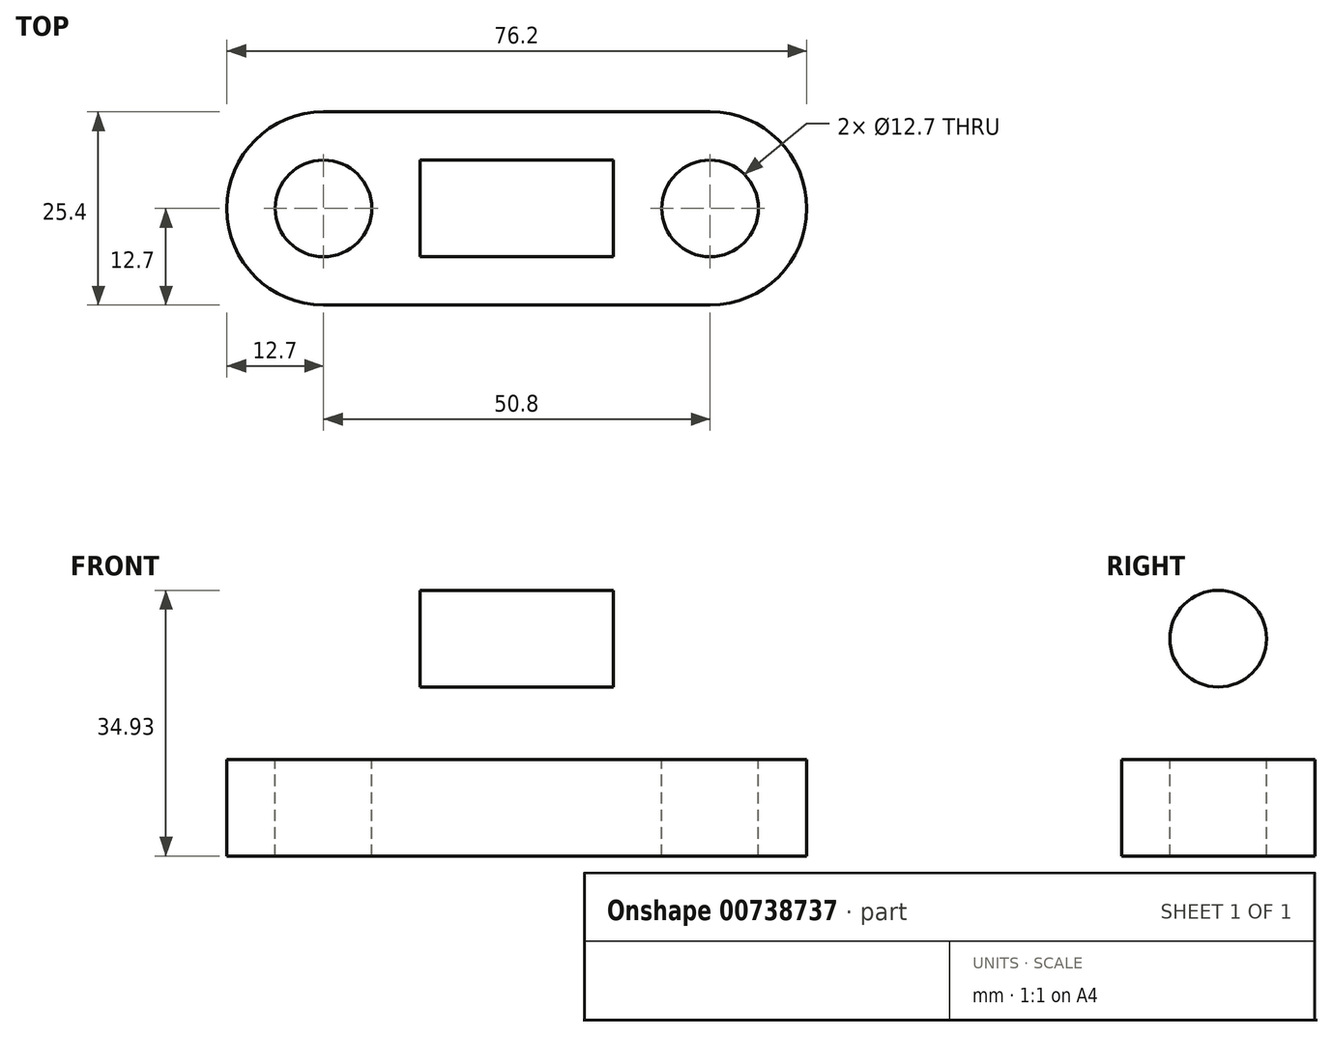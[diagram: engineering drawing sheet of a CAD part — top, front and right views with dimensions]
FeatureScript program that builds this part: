
annotation { "Feature Type Name" : "Feature", "Feature Type Description" : "" }
export const myFeature = defineFeature(function(context is Context, id is Id, definition is map)
    precondition{}
    {
        {
            var Q0;
            Q0=qCreatedBy(makeId("Front.planeOp"),FACE);
            var sketch = newSketch(context, id + "F0", { "sketchPlane" : qUnion([Q0])});
            skLineSegment(sketch, "E0", {"start": v(0, 0) * mm, "end": v(76.2, 0) * mm});
            skLineSegment(sketch, "E1", {"start": v(76.2, 0) * mm, "end": v(76.2, 12.7) * mm});
            skLineSegment(sketch, "E2", {"start": v(76.2, 12.7) * mm, "end": v(50.8, 12.7) * mm});
            skLineSegment(sketch, "E3", {"start": v(50.8, 12.7) * mm, "end": v(50.8, 44.45) * mm});
            skLineSegment(sketch, "E4", {"start": v(50.8, 44.45) * mm, "end": v(25.4, 44.45) * mm});
            skLineSegment(sketch, "E5", {"start": v(25.4, 44.45) * mm, "end": v(25.4, 12.7) * mm});
            skLineSegment(sketch, "E6", {"start": v(25.4, 12.7) * mm, "end": v(0, 12.7) * mm});
            skLineSegment(sketch, "E7", {"start": v(0, 12.7) * mm, "end": v(0, 0) * mm});
            skSolve(sketch);
        }
        {
            var Q0;
            Q0 = qSketchRegion(id + "F0", true);
            extrude(context, id + "F1", {"entities" : qUnion([Q0]), "depth" : 25.4 * mm, "offsetDistance" : 25.4 * mm});
        }
        {
            var Q0;
            Q0=makeQuery(id+"F1.opExtrude","SWEPT_FACE",FACE,{"disambiguationData":[OSD([sQuery(id+"F0.wireOp",EDGE,"E3")])]});
            var sketch = newSketch(context, id + "F2", { "sketchPlane" : qUnion([Q0])});
            skLineSegment(sketch, "E8", {"start": v(-25.4, 28.58) * mm, "end": v(0, 28.58) * mm});
            skCircle(sketch, "E9", {"center": v(-12.7, 28.58) * mm, "radius": 6.35 * mm});
            skArc(sketch, "E10", {"start": v(0, 28.58) * mm, "mid": v(-12.7, 41.27) * mm, "end": v(-25.4, 28.58) * mm});
            skSolve(sketch);
        }
        {
            var Q0;
            {var subQ0=sQuery(id+"F2.wireOp",EDGE,"E9");var subQ1=sQuery(id+"F2.wireOp",EDGE,"E8");var subQ2=makeQuery(id+"F2.imprint","INTERSECT",VERTEX,{"disambiguationData":[OD(0.0)],"derivedFrom":[subQ1,subQ0]});Q0=makeQuery(id+"F2.imprint","IMPRINT",FACE,{"disambiguationData":[TD([[makeQuery(id+"F2.imprint","IMPRINT",EDGE,{"disambiguationData":[TD([[subQ2,-1.0]])],"derivedFrom":subQ1}),1.0]])]});}
            var Q1;
            {var subQ0=sQuery(id+"F2.wireOp",EDGE,"E9");var subQ1=sQuery(id+"F2.wireOp",EDGE,"E8");var subQ2=makeQuery(id+"F2.imprint","INTERSECT",VERTEX,{"disambiguationData":[OD(0.0)],"derivedFrom":[subQ1,subQ0]});Q1=makeQuery(id+"F2.imprint","IMPRINT",FACE,{"disambiguationData":[TD([[makeQuery(id+"F2.imprint","IMPRINT",EDGE,{"disambiguationData":[TD([[subQ2,-1.0]])],"derivedFrom":subQ1}),-1.0]])]});}
            var Q2;
            {var subQ0=sQuery(id+"F2.wireOp",EDGE,"E10");Q2=makeQuery(id+"F2.imprint","IMPRINT",FACE,{"disambiguationData":[TD([[makeQuery(id+"F2.imprint","IMPRINT",EDGE,{"derivedFrom":subQ0}),-1.0]])]});}
            extrude(context, id + "F3", {"entities" : qUnion([Q0, Q1, Q2]), "operationType" : NewBodyOperationType.REMOVE, "endBound" : BoundingType.THROUGH_ALL, "oppositeDirection" : true, "depth" : 25.4 * mm, "offsetDistance" : 25.4 * mm});
        }
        {
            var Q0;
            Q0=makeQuery(id+"F1.opExtrude","SWEPT_FACE",FACE,{"disambiguationData":[OSD([sQuery(id+"F0.wireOp",EDGE,"E6")])]});
            var sketch = newSketch(context, id + "F4", { "sketchPlane" : qUnion([Q0])});
            skLineSegment(sketch, "E11", {"start": v(12.7, -25.4) * mm, "end": v(12.7, 0) * mm});
            skCircle(sketch, "E12", {"center": v(12.7, -12.7) * mm, "radius": 6.35 * mm});
            skArc(sketch, "E13", {"start": v(12.7, 0) * mm, "mid": v(0, -12.7) * mm, "end": v(12.7, -25.4) * mm});
            skSolve(sketch);
        }
        {
            var Q0;
            {var subQ0=sQuery(id+"F4.wireOp",EDGE,"E12");var subQ1=sQuery(id+"F4.wireOp",EDGE,"E11");var subQ2=makeQuery(id+"F4.imprint","INTERSECT",VERTEX,{"disambiguationData":[OD(0.0)],"derivedFrom":[subQ1,subQ0]});Q0=makeQuery(id+"F4.imprint","IMPRINT",FACE,{"disambiguationData":[TD([[makeQuery(id+"F4.imprint","IMPRINT",EDGE,{"disambiguationData":[TD([[subQ2,-1.0]])],"derivedFrom":subQ1}),1.0]])]});}
            var Q1;
            {var subQ0=sQuery(id+"F4.wireOp",EDGE,"E12");var subQ1=sQuery(id+"F4.wireOp",EDGE,"E11");var subQ2=makeQuery(id+"F4.imprint","INTERSECT",VERTEX,{"disambiguationData":[OD(0.0)],"derivedFrom":[subQ1,subQ0]});Q1=makeQuery(id+"F4.imprint","IMPRINT",FACE,{"disambiguationData":[TD([[makeQuery(id+"F4.imprint","IMPRINT",EDGE,{"disambiguationData":[TD([[subQ2,-1.0]])],"derivedFrom":subQ1}),-1.0]])]});}
            var Q2;
            {var subQ0=sQuery(id+"F4.wireOp",EDGE,"E13");var subQ1=sQuery(id+"F0.wireOp",EDGE,"E6");var subQ2=makeQuery(id+"F1.opExtrude","CAP_EDGE",EDGE,{"disambiguationData":[OSD([subQ1])],"isStart":true});var subQ3=makeQuery(id+"F4.imprint","INTERSECT",VERTEX,{"derivedFrom":[subQ2,sQuery(id+"F4.wireOp",EDGE,"E11"),subQ0]});Q2=makeQuery(id+"F4.imprint","IMPRINT",FACE,{"disambiguationData":[TD([[makeQuery(id+"F4.imprint","IMPRINT",EDGE,{"disambiguationData":[TD([[subQ3,-1.0]])],"derivedFrom":subQ0}),-1.0]])]});}
            var Q3;
            {var subQ0=sQuery(id+"F4.wireOp",EDGE,"E13");var subQ1=sQuery(id+"F0.wireOp",EDGE,"E6");var subQ2=makeQuery(id+"F1.opExtrude","CAP_EDGE",EDGE,{"disambiguationData":[OSD([subQ1])],"isStart":false});var subQ3=makeQuery(id+"F4.imprint","INTERSECT",VERTEX,{"derivedFrom":[subQ2,sQuery(id+"F4.wireOp",EDGE,"E11"),subQ0]});Q3=makeQuery(id+"F4.imprint","IMPRINT",FACE,{"disambiguationData":[TD([[makeQuery(id+"F4.imprint","IMPRINT",EDGE,{"disambiguationData":[TD([[subQ3,1.0]])],"derivedFrom":subQ0}),-1.0]])]});}
            extrude(context, id + "F5", {"entities" : qUnion([Q0, Q1, Q2, Q3]), "operationType" : NewBodyOperationType.REMOVE, "endBound" : BoundingType.THROUGH_ALL, "oppositeDirection" : true, "depth" : 25.4 * mm, "offsetDistance" : 25.4 * mm});
        }
        {
            var Q0;
            Q0=makeQuery(id+"F1.opExtrude","SWEPT_FACE",FACE,{"disambiguationData":[OSD([sQuery(id+"F0.wireOp",EDGE,"E2")])]});
            var sketch = newSketch(context, id + "F6", { "sketchPlane" : qUnion([Q0])});
            skLineSegment(sketch, "E14", {"start": v(63.5, 0) * mm, "end": v(63.5, -25.4) * mm});
            skCircle(sketch, "E15", {"center": v(63.5, -12.7) * mm, "radius": 6.35 * mm});
            skArc(sketch, "E16", {"start": v(63.5, -25.4) * mm, "mid": v(76.2, -12.7) * mm, "end": v(63.5, 0) * mm});
            skSolve(sketch);
        }
        {
            var Q0;
            {var subQ0=sQuery(id+"F6.wireOp",EDGE,"E15");var subQ1=sQuery(id+"F6.wireOp",EDGE,"E14");var subQ2=makeQuery(id+"F6.imprint","INTERSECT",VERTEX,{"disambiguationData":[OD(0.0)],"derivedFrom":[subQ1,subQ0]});Q0=makeQuery(id+"F6.imprint","IMPRINT",FACE,{"disambiguationData":[TD([[makeQuery(id+"F6.imprint","IMPRINT",EDGE,{"disambiguationData":[TD([[subQ2,-1.0]])],"derivedFrom":subQ1}),-1.0]])]});}
            var Q1;
            {var subQ0=sQuery(id+"F6.wireOp",EDGE,"E15");var subQ1=sQuery(id+"F6.wireOp",EDGE,"E14");var subQ2=makeQuery(id+"F6.imprint","INTERSECT",VERTEX,{"disambiguationData":[OD(0.0)],"derivedFrom":[subQ1,subQ0]});Q1=makeQuery(id+"F6.imprint","IMPRINT",FACE,{"disambiguationData":[TD([[makeQuery(id+"F6.imprint","IMPRINT",EDGE,{"disambiguationData":[TD([[subQ2,-1.0]])],"derivedFrom":subQ1}),1.0]])]});}
            var Q2;
            {var subQ0=sQuery(id+"F6.wireOp",EDGE,"E16");var subQ1=sQuery(id+"F0.wireOp",EDGE,"E2");var subQ2=makeQuery(id+"F1.opExtrude","CAP_EDGE",EDGE,{"disambiguationData":[OSD([subQ1])],"isStart":true});var subQ3=makeQuery(id+"F6.imprint","INTERSECT",VERTEX,{"derivedFrom":[subQ2,sQuery(id+"F6.wireOp",EDGE,"E14"),subQ0]});Q2=makeQuery(id+"F6.imprint","IMPRINT",FACE,{"disambiguationData":[TD([[makeQuery(id+"F6.imprint","IMPRINT",EDGE,{"disambiguationData":[TD([[subQ3,1.0]])],"derivedFrom":subQ0}),-1.0]])]});}
            var Q3;
            {var subQ0=sQuery(id+"F6.wireOp",EDGE,"E16");var subQ1=sQuery(id+"F0.wireOp",EDGE,"E2");var subQ2=makeQuery(id+"F1.opExtrude","CAP_EDGE",EDGE,{"disambiguationData":[OSD([subQ1])],"isStart":false});var subQ3=makeQuery(id+"F6.imprint","INTERSECT",VERTEX,{"derivedFrom":[subQ2,sQuery(id+"F6.wireOp",EDGE,"E14"),subQ0]});Q3=makeQuery(id+"F6.imprint","IMPRINT",FACE,{"disambiguationData":[TD([[makeQuery(id+"F6.imprint","IMPRINT",EDGE,{"disambiguationData":[TD([[subQ3,-1.0]])],"derivedFrom":subQ0}),-1.0]])]});}
            extrude(context, id + "F7", {"entities" : qUnion([Q0, Q1, Q2, Q3]), "operationType" : NewBodyOperationType.REMOVE, "oppositeDirection" : true, "depth" : 25.4 * mm, "offsetDistance" : 25.4 * mm});
        }
    });
